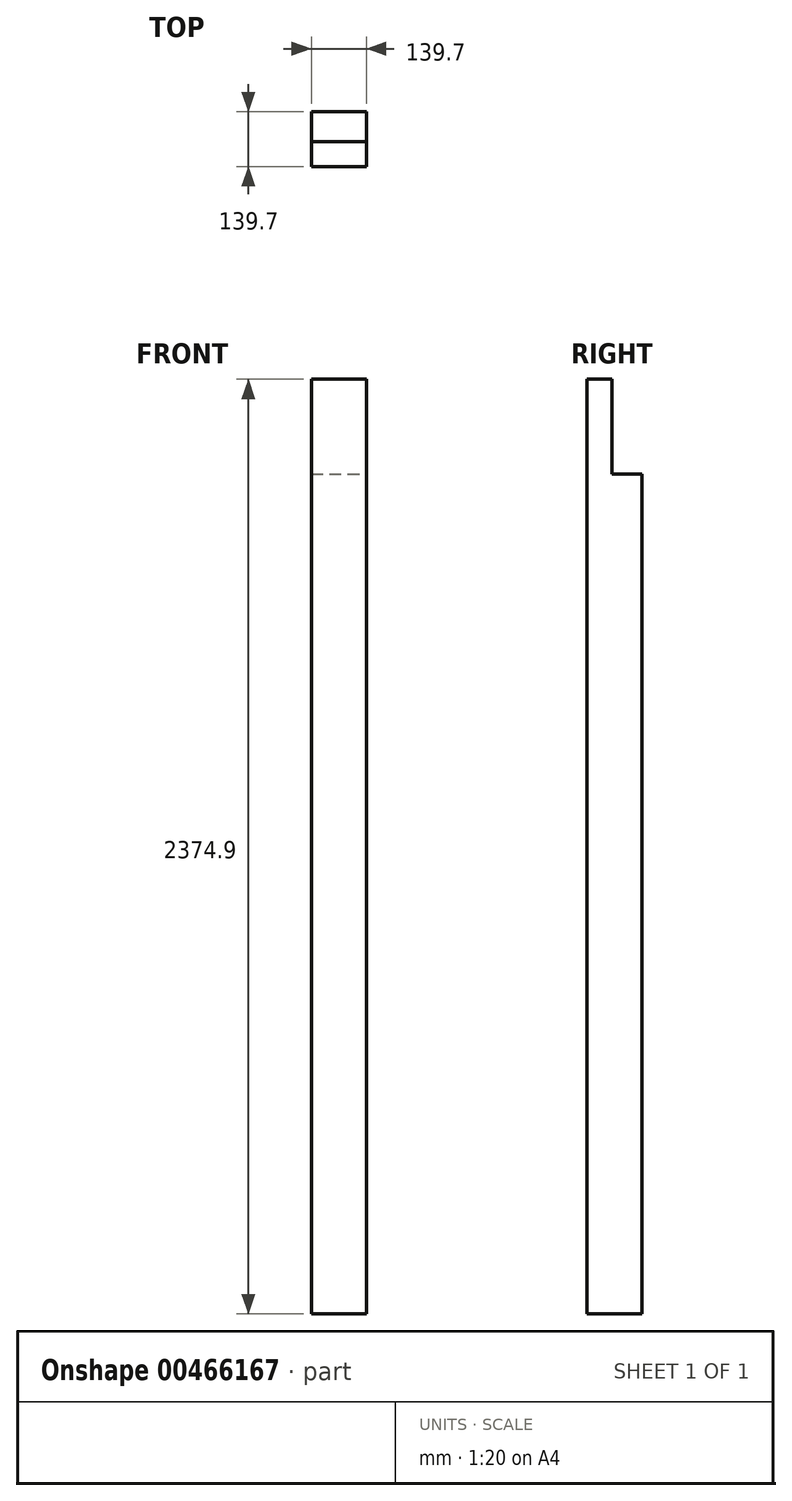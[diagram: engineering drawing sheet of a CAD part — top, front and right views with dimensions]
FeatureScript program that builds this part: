
annotation { "Feature Type Name" : "Feature", "Feature Type Description" : "" }
export const myFeature = defineFeature(function(context is Context, id is Id, definition is map)
    precondition{}
    {
        {
            var Q0;
            Q0=qCreatedBy(makeId("Top.planeOp"),FACE);
            var sketch = newSketch(context, id + "F0", { "sketchPlane" : qUnion([Q0])});
            skLineSegment(sketch, "E0.bottom", {"start": v(-43.75, 59.21) * mm, "end": v(95.95, 59.21) * mm});
            skLineSegment(sketch, "E0.top", {"start": v(-43.75, -80.49) * mm, "end": v(95.95, -80.49) * mm});
            skLineSegment(sketch, "E0.left", {"start": v(-43.75, 59.21) * mm, "end": v(-43.75, -80.49) * mm});
            skLineSegment(sketch, "E0.right", {"start": v(95.95, 59.21) * mm, "end": v(95.95, -80.49) * mm});
            skSolve(sketch);
        }
        {
            var Q0;
            Q0=makeQuery(id+"F0.imprint","IMPRINT",FACE,{"disambiguationData":[TD([[makeQuery(id+"F0.imprint","IMPRINT",EDGE,{"derivedFrom":sQuery(id+"F0.wireOp",EDGE,"E0.bottom")}),-1.0]])]});
            extrude(context, id + "F1", {"entities" : qUnion([Q0]), "depth" : 2374.9 * mm});
        }
        {
            var Q0;
            Q0=makeQuery(id+"F1.opExtrude","SWEPT_FACE",FACE,{"disambiguationData":[OSD([sQuery(id+"F0.wireOp",EDGE,"E0.right")])]});
            var sketch = newSketch(context, id + "F2", { "sketchPlane" : qUnion([Q0])});
            skLineSegment(sketch, "E1.bottom", {"start": v(-16.99, 2374.9) * mm, "end": v(59.21, 2374.9) * mm});
            skLineSegment(sketch, "E1.top", {"start": v(-16.99, 2133.6) * mm, "end": v(59.21, 2133.6) * mm});
            skLineSegment(sketch, "E1.left", {"start": v(-16.99, 2374.9) * mm, "end": v(-16.99, 2133.6) * mm});
            skLineSegment(sketch, "E1.right", {"start": v(59.21, 2374.9) * mm, "end": v(59.21, 2133.6) * mm});
            skSolve(sketch);
        }
        {
            var Q0;
            Q0=makeQuery(id+"F2.imprint","IMPRINT",FACE,{"disambiguationData":[TD([[makeQuery(id+"F2.imprint","IMPRINT",EDGE,{"derivedFrom":sQuery(id+"F2.wireOp",EDGE,"E1.bottom")}),1.0]])]});
            extrude(context, id + "F3", {"entities" : qUnion([Q0]), "operationType" : NewBodyOperationType.REMOVE, "endBound" : BoundingType.THROUGH_ALL, "oppositeDirection" : true, "depth" : 25.4 * mm});
        }
    });
